annotation { "Feature Type Name" : "Feature", "Feature Type Description" : "" }
export const myFeature = defineFeature(function(context is Context, id is Id, definition is map)
    precondition{}
    {
        {
            var Q0;
            Q0=qCreatedBy(makeId("Top.planeOp"),FACE);
            var sketch = newSketch(context, id + "F0", { "sketchPlane" : qUnion([Q0])});
            skText(sketch, "E0", { "text": "Arca Somni", "fontName": "OpenSans-Regular.ttf"});
            const initialGuessF0  = {"E0": [-0.05069, -0.00489, 1, 0, 0.03321]};
            skSetInitialGuess(sketch, initialGuessF0);
            skSolve(sketch);
        }
        {
            var Q0;
            Q0 = qSketchRegion(id + "F0", true);
            extrude(context, id + "F1", {"entities" : qUnion([Q0]), "oppositeDirection" : true, "depth" : 25.4 * mm, "offsetDistance" : 25.4 * mm});
        }
        {
            var Q0;
            Q0=qCreatedBy(makeId("Top.planeOp"),FACE);
            var sketch = newSketch(context, id + "F2", { "sketchPlane" : qUnion([Q0])});
            skPoint(sketch, "E1.0", {"position": v(-21.5, -4.89) * mm});
            skPoint(sketch, "E2.0", {"position": v(-17.53, 19.8) * mm});
            skLineSegment(sketch, "E3", {"start": v(-21.5, -4.89) * mm, "end": v(-17.53, 7.02) * mm});
            skLineSegment(sketch, "E4", {"start": v(-19.32, 7.02) * mm, "end": v(-22.4, -2.24) * mm});
            skLineSegment(sketch, "E5", {"start": v(-22.4, -2.24) * mm, "end": v(-21.5, -4.89) * mm});
            skLineSegment(sketch, "E6", {"start": v(-19.32, 7.02) * mm, "end": v(-17.53, 12.4) * mm});
            skLineSegment(sketch, "E7", {"start": v(-17.53, 12.4) * mm, "end": v(-17.53, 7.02) * mm});
            skSolve(sketch);
        }
        {
            var Q0;
            Q0=makeQuery(id+"F2.imprint","IMPRINT",FACE,{"disambiguationData":[TD([[makeQuery(id+"F2.imprint","IMPRINT",EDGE,{"derivedFrom":sQuery(id+"F2.wireOp",EDGE,"E3")}),1.0]])]});
            extrude(context, id + "F3", {"entities" : qUnion([Q0]), "oppositeDirection" : true, "depth" : 25.4 * mm, "offsetDistance" : 25.4 * mm});
        }
    });